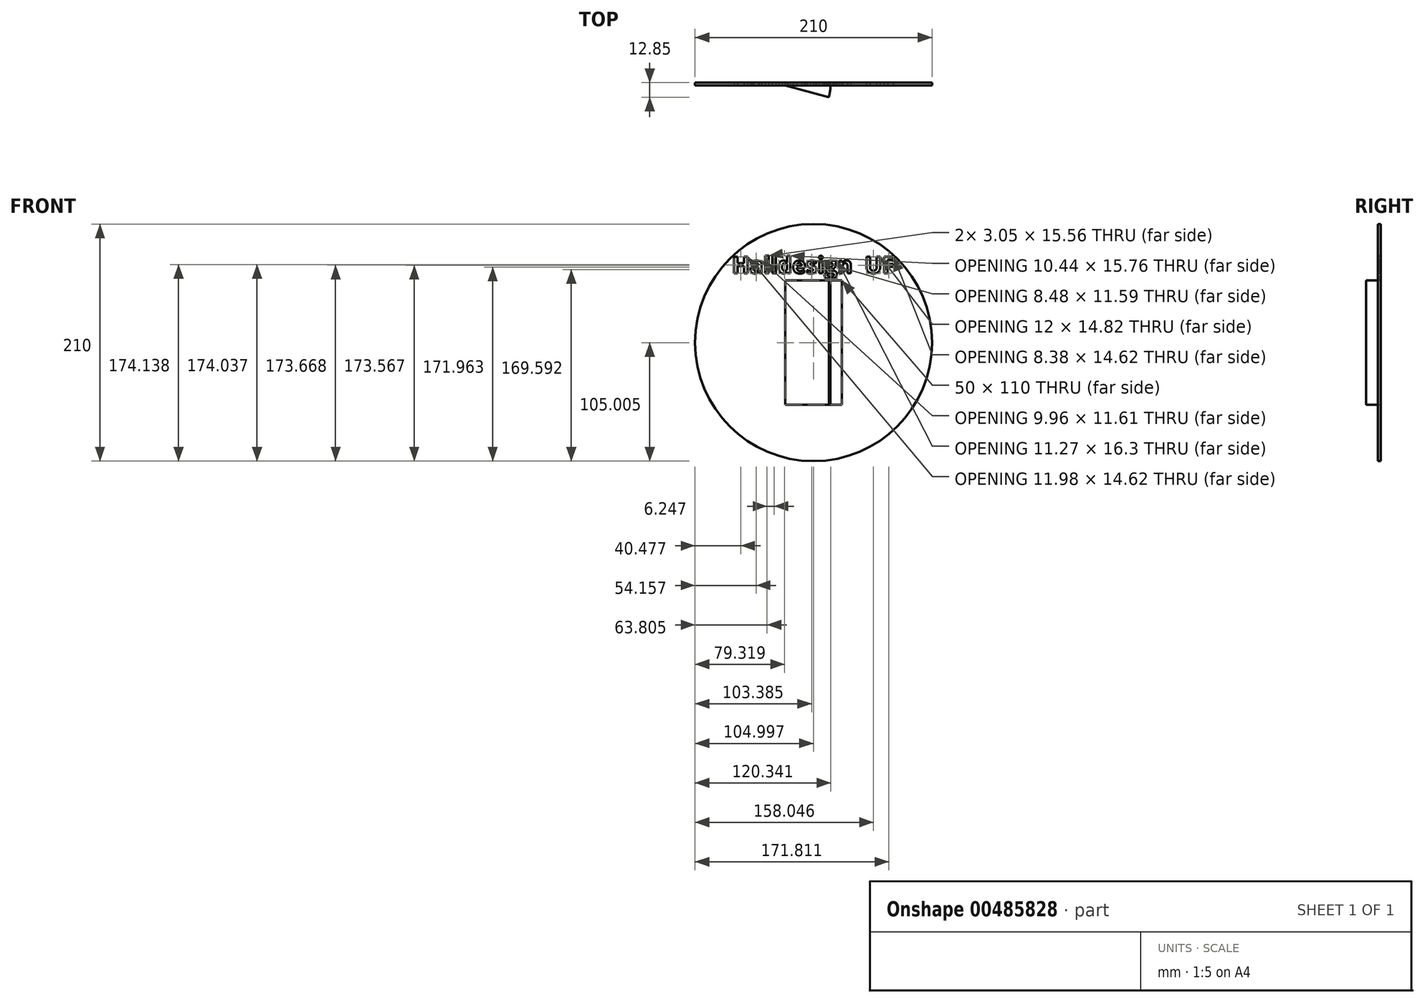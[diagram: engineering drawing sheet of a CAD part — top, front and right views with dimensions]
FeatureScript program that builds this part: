
annotation { "Feature Type Name" : "Feature", "Feature Type Description" : "" }
export const myFeature = defineFeature(function(context is Context, id is Id, definition is map)
    precondition{}
    {
        {
            var Q0;
            Q0=qCreatedBy(makeId("Front.planeOp"),FACE);
            var sketch = newSketch(context, id + "F0", { "sketchPlane" : qUnion([Q0])});
            skCircle(sketch, "E0", {"center": v(-56.72, 37.41) * mm, "radius": 105 * mm});
            skLineSegment(sketch, "E1.bottom", {"start": v(-81.72, 92.41) * mm, "end": v(-31.72, 92.41) * mm});
            skLineSegment(sketch, "E1.top", {"start": v(-81.72, -17.59) * mm, "end": v(-31.72, -17.59) * mm});
            skLineSegment(sketch, "E1.right", {"start": v(-31.72, 92.41) * mm, "end": v(-31.72, -17.59) * mm});
            skLineSegment(sketch, "E2", {"start": v(-81.72, 92.41) * mm, "end": v(-81.72, -17.59) * mm});
            skLineSegment(sketch, "E3", {"start": v(-81.72, 92.41) * mm, "end": v(-41.72, 92.41) * mm});
            skLineSegment(sketch, "E4", {"start": v(-41.72, 92.41) * mm, "end": v(-41.72, -17.59) * mm});
            skLineSegment(sketch, "E5", {"start": v(-41.72, -17.59) * mm, "end": v(-81.72, -17.59) * mm});
            skSolve(sketch);
        }
        {
            var Q0;
            Q0=makeQuery(id+"F0.imprint","IMPRINT",FACE,{"disambiguationData":[TD([[makeQuery(id+"F0.imprint","IMPRINT",EDGE,{"derivedFrom":sQuery(id+"F0.wireOp",EDGE,"E2")}),1.0]])]});
            extrude(context, id + "F1", {"entities" : qUnion([Q0]), "depth" : 2.5 * mm});
        }
        {
            var Q0;
            Q0 = qSketchRegion(id + "F0", true);
            extrude(context, id + "F2", {"entities" : qUnion([Q0]), "depth" : 2.5 * mm});
        }
        {
            var Q0;
            Q0=makeQuery(id+"F1.opExtrude","CAP_FACE",FACE,{"disambiguationData":[OSD([sQuery(id+"F0.wireOp",EDGE,"E2"),sQuery(id+"F0.wireOp",EDGE,"E3"),sQuery(id+"F0.wireOp",EDGE,"E4"),sQuery(id+"F0.wireOp",EDGE,"E5")])],"isStart":false});
            var sketch = newSketch(context, id + "F3", { "sketchPlane" : qUnion([Q0])});
            skLineSegment(sketch, "E6", {"start": v(-81.72, 119.52) * mm, "end": v(-81.72, -78.8) * mm, "construction": true});
            skSolve(sketch);
        }
        {
            var Q0;
            Q0=makeQuery(id+"F3.imprint","IMPRINT",FACE,{"disambiguationData":[TD([[makeQuery(id+"F3.imprint","IMPRINT",EDGE,{"derivedFrom":makeQuery(id+"F1.opExtrude","CAP_EDGE",EDGE,{"disambiguationData":[OSD([sQuery(id+"F0.wireOp",EDGE,"E2")])],"isStart":false})}),1.0]])]});
            var Q1;
            Q1 = qSketchRegion(id + "F6", true);
            var Q2;
            Q2=sQuery(id+"F3.wireOp",EDGE,"E6");
            revolve(context, id + "F4", {"entities" : qUnion([Q0, Q1]), "axis" : qUnion([Q2]), "revolveType" : RevolveType.ONE_DIRECTION, "angle" : 15 * degree});
        }
        {
            var Q0;
            Q0=makeQuery(id+"F2.opExtrude","CAP_FACE",FACE,{"disambiguationData":[OSD([sQuery(id+"F0.wireOp",EDGE,"E0"),sQuery(id+"F0.wireOp",EDGE,"E1.bottom"),sQuery(id+"F0.wireOp",EDGE,"E1.top"),sQuery(id+"F0.wireOp",EDGE,"E1.right"),sQuery(id+"F0.wireOp",EDGE,"E2"),sQuery(id+"F0.wireOp",EDGE,"E3"),sQuery(id+"F0.wireOp",EDGE,"E5")])],"isStart":false});
            var sketch = newSketch(context, id + "F5", { "sketchPlane" : qUnion([Q0])});
            skText(sketch, "E7", { "text": "Halldesign  UF", "fontName": "OpenSans-Bold.ttf"});
            const initialGuessF5  = {"E7": [-0.12907, 0.09877, 1, 0, 0.01474]};
            skSetInitialGuess(sketch, initialGuessF5);
            skSolve(sketch);
        }
        {
            var Q0;
            Q0=makeQuery(id+"F5.imprint","IMPRINT",FACE,{"disambiguationData":[TD([[makeQuery(id+"F5.imprint","IMPRINT",EDGE,{"derivedFrom":sQuery(id+"F5.wireOp",EDGE,"E7.sketch_text.stroke-0")}),1.0]])]});
            var sketch = newSketch(context, id + "F6", { "sketchPlane" : qUnion([Q0])});
            skSolve(sketch);
        }
        {
            var Q0;
            Q0 = qSketchRegion(id + "F5", true);
            extrude(context, id + "F7", {"entities" : qUnion([Q0]), "operationType" : NewBodyOperationType.REMOVE, "oppositeDirection" : true, "depth" : 50 * mm});
        }
    });
